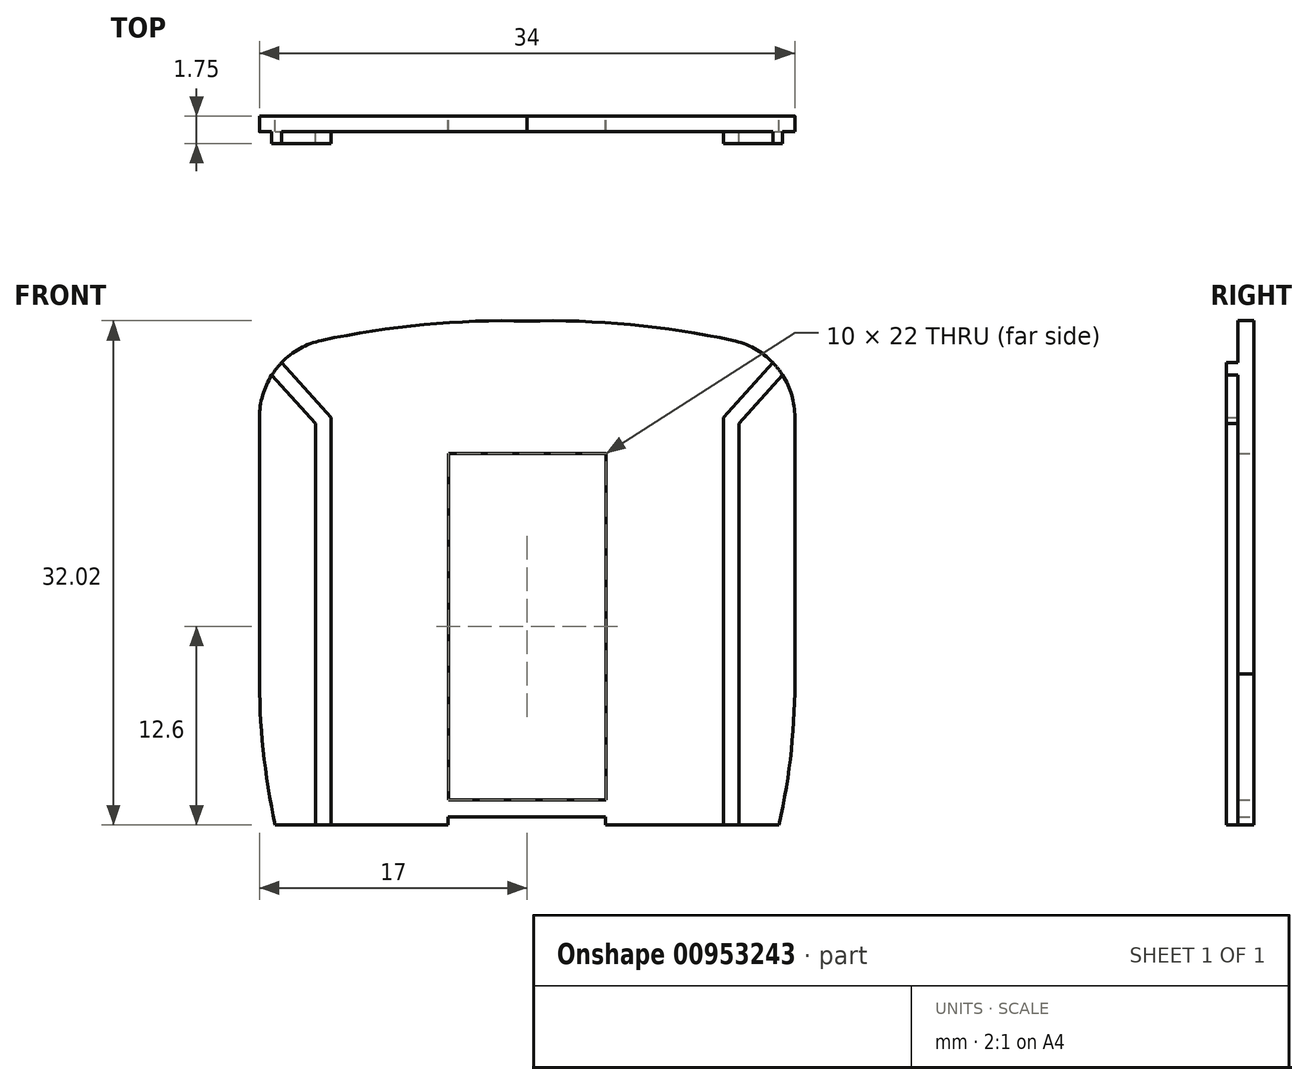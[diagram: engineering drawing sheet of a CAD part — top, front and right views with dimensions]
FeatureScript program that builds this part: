
annotation { "Feature Type Name" : "Feature", "Feature Type Description" : "" }
export const myFeature = defineFeature(function(context is Context, id is Id, definition is map)
    precondition{}
    {
        {
            var Q0;
            Q0=qCreatedBy(makeId("Front.planeOp"),FACE);
            var sketch = newSketch(context, id + "F0", { "sketchPlane" : qUnion([Q0])});
            skLineSegment(sketch, "E0", {"start": v(0, -18.67) * mm, "end": v(0, -38.67) * mm, "construction": true});
            skLineSegment(sketch, "E1", {"start": v(0, 0) * mm, "end": v(0, -9.6) * mm});
            skArc(sketch, "E2", {"start": v(16, -9.6) * mm, "mid": v(16.77, -4.83) * mm, "end": v(17, 0) * mm});
            skArc(sketch, "E3.MirrorCS", {"start": v(-16, -9.6) * mm, "mid": v(-16.77, -4.83) * mm, "end": v(-17, 0) * mm});
            skLineSegment(sketch, "E4", {"start": v(-17, 0) * mm, "end": v(-17, 16.28) * mm});
            skLineSegment(sketch, "E5", {"start": v(17, 0) * mm, "end": v(17, 16.28) * mm});
            skArc(sketch, "E6", {"start": v(13.06, 21.17) * mm, "mid": v(6.57, 22.18) * mm, "end": v(0, 22.4) * mm});
            skArc(sketch, "E7.MirrorCS", {"start": v(-13.06, 21.17) * mm, "mid": v(-6.57, 22.18) * mm, "end": v(0, 22.4) * mm});
            skPoint(sketch, "E8.visualSharp", {"position": v(-17, 20.16) * mm});
            skArc(sketch, "E8.filletArc", {"start": v(-13.06, 21.17) * mm, "mid": v(-15.9, 19.42) * mm, "end": v(-17, 16.28) * mm});
            skPoint(sketch, "E9.visualSharp", {"position": v(17, 20.16) * mm});
            skArc(sketch, "E9.filletArc", {"start": v(17, 16.28) * mm, "mid": v(15.9, 19.42) * mm, "end": v(13.06, 21.17) * mm});
            skLineSegment(sketch, "E10", {"start": v(-16, -9.6) * mm, "end": v(16, -9.6) * mm});
            skLineSegment(sketch, "E11.bottom", {"start": v(5, -8) * mm, "end": v(-5, -8) * mm});
            skLineSegment(sketch, "E11.top", {"start": v(5, 14) * mm, "end": v(-5, 14) * mm});
            skLineSegment(sketch, "E11.right", {"start": v(-5, -8) * mm, "end": v(-5, 14) * mm});
            skLineSegment(sketch, "E12", {"start": v(5, 14) * mm, "end": v(5, -8) * mm});
            skLineSegment(sketch, "E13.bottom", {"start": v(-5.02, -9.6) * mm, "end": v(4.96, -9.6) * mm});
            skLineSegment(sketch, "E13.top", {"start": v(-5.02, -9.1) * mm, "end": v(4.96, -9.1) * mm});
            skLineSegment(sketch, "E13.left", {"start": v(-5.02, -9.6) * mm, "end": v(-5.02, -9.1) * mm});
            skLineSegment(sketch, "E13.right", {"start": v(4.96, -9.6) * mm, "end": v(4.96, -9.1) * mm});
            skSolve(sketch);
        }
        {
            var Q0;
            Q0 = qSketchRegion(id + "F0", true);
            extrude(context, id + "F1", {"entities" : qUnion([Q0]), "depth" : 1 * mm, "offsetDistance" : 25 * mm});
        }
        {
            var Q0;
            {var subQ5=sQuery(id+"F0.wireOp",EDGE,"E13.left");Q0=makeQuery(id+"F0.imprint","IMPRINT",FACE,{"disambiguationData":[TD([[makeQuery(id+"F0.imprint","IMPRINT",EDGE,{"derivedFrom":subQ5}),-1.0]])]});}
            var Q1;
            {var subQ5=sQuery(id+"F0.wireOp",EDGE,"E13.right");Q1=makeQuery(id+"F0.imprint","IMPRINT",FACE,{"disambiguationData":[TD([[makeQuery(id+"F0.imprint","IMPRINT",EDGE,{"derivedFrom":subQ5}),1.0]])]});}
            extrude(context, id + "F2", {"entities" : qUnion([Q0, Q1]), "operationType" : NewBodyOperationType.REMOVE, "depth" : 8.4 * mm, "offsetDistance" : 25 * mm});
        }
        {
            var Q0;
            Q0=makeQuery(id+"F1.opExtrude","CAP_FACE",FACE,{"disambiguationData":[OSD([sQuery(id+"F0.wireOp",EDGE,"E2"),sQuery(id+"F0.wireOp",EDGE,"E3.MirrorCS"),sQuery(id+"F0.wireOp",EDGE,"E4"),sQuery(id+"F0.wireOp",EDGE,"E5"),sQuery(id+"F0.wireOp",EDGE,"E6"),sQuery(id+"F0.wireOp",EDGE,"E7.MirrorCS"),sQuery(id+"F0.wireOp",EDGE,"E8.filletArc"),sQuery(id+"F0.wireOp",EDGE,"E9.filletArc"),sQuery(id+"F0.wireOp",EDGE,"E10"),sQuery(id+"F0.wireOp",EDGE,"E11.bottom"),sQuery(id+"F0.wireOp",EDGE,"E11.top"),sQuery(id+"F0.wireOp",EDGE,"E11.right"),sQuery(id+"F0.wireOp",EDGE,"E12"),sQuery(id+"F0.wireOp",EDGE,"E13.bottom")])],"isStart":false});
            var sketch = newSketch(context, id + "F3", { "sketchPlane" : qUnion([Q0])});
            skLineSegment(sketch, "E14", {"start": v(-12.45, -9.6) * mm, "end": v(-12.45, 16.28) * mm});
            skLineSegment(sketch, "E15", {"start": v(-12.45, 16.28) * mm, "end": v(-15.6, 19.76) * mm});
            skLineSegment(sketch, "E16", {"start": v(0, 0) * mm, "end": v(0, 14) * mm, "construction": true});
            skLineSegment(sketch, "E17.MirrorCS", {"start": v(12.45, -9.6) * mm, "end": v(12.45, 16.28) * mm});
            skLineSegment(sketch, "E18.0", {"start": v(-13.45, 15.9) * mm, "end": v(-16.34, 19.09) * mm});
            skLineSegment(sketch, "E18.1", {"start": v(-13.45, -9.6) * mm, "end": v(-13.45, 15.9) * mm});
            skLineSegment(sketch, "E19.MirrorCS", {"start": v(13.45, 15.9) * mm, "end": v(16.34, 19.09) * mm});
            skLineSegment(sketch, "E20.MirrorCS", {"start": v(13.45, -9.6) * mm, "end": v(13.45, 15.9) * mm});
            skLineSegment(sketch, "E21.MirrorCS", {"start": v(12.45, 16.28) * mm, "end": v(15.6, 19.76) * mm});
            skSolve(sketch);
        }
        {
            var Q0;
            {var subQ6=sQuery(id+"F3.wireOp",EDGE,"E14");Q0=makeQuery(id+"F3.imprint","IMPRINT",FACE,{"disambiguationData":[TD([[makeQuery(id+"F3.imprint","IMPRINT",EDGE,{"derivedFrom":subQ6}),1.0]])]});}
            var Q1;
            {var subQ6=sQuery(id+"F3.wireOp",EDGE,"E17.MirrorCS");Q1=makeQuery(id+"F3.imprint","IMPRINT",FACE,{"disambiguationData":[TD([[makeQuery(id+"F3.imprint","IMPRINT",EDGE,{"derivedFrom":subQ6}),-1.0]])]});}
            extrude(context, id + "F4", {"entities" : qUnion([Q0, Q1]), "operationType" : NewBodyOperationType.ADD, "depth" : 0.75 * mm, "offsetDistance" : 25 * mm});
        }
    });
